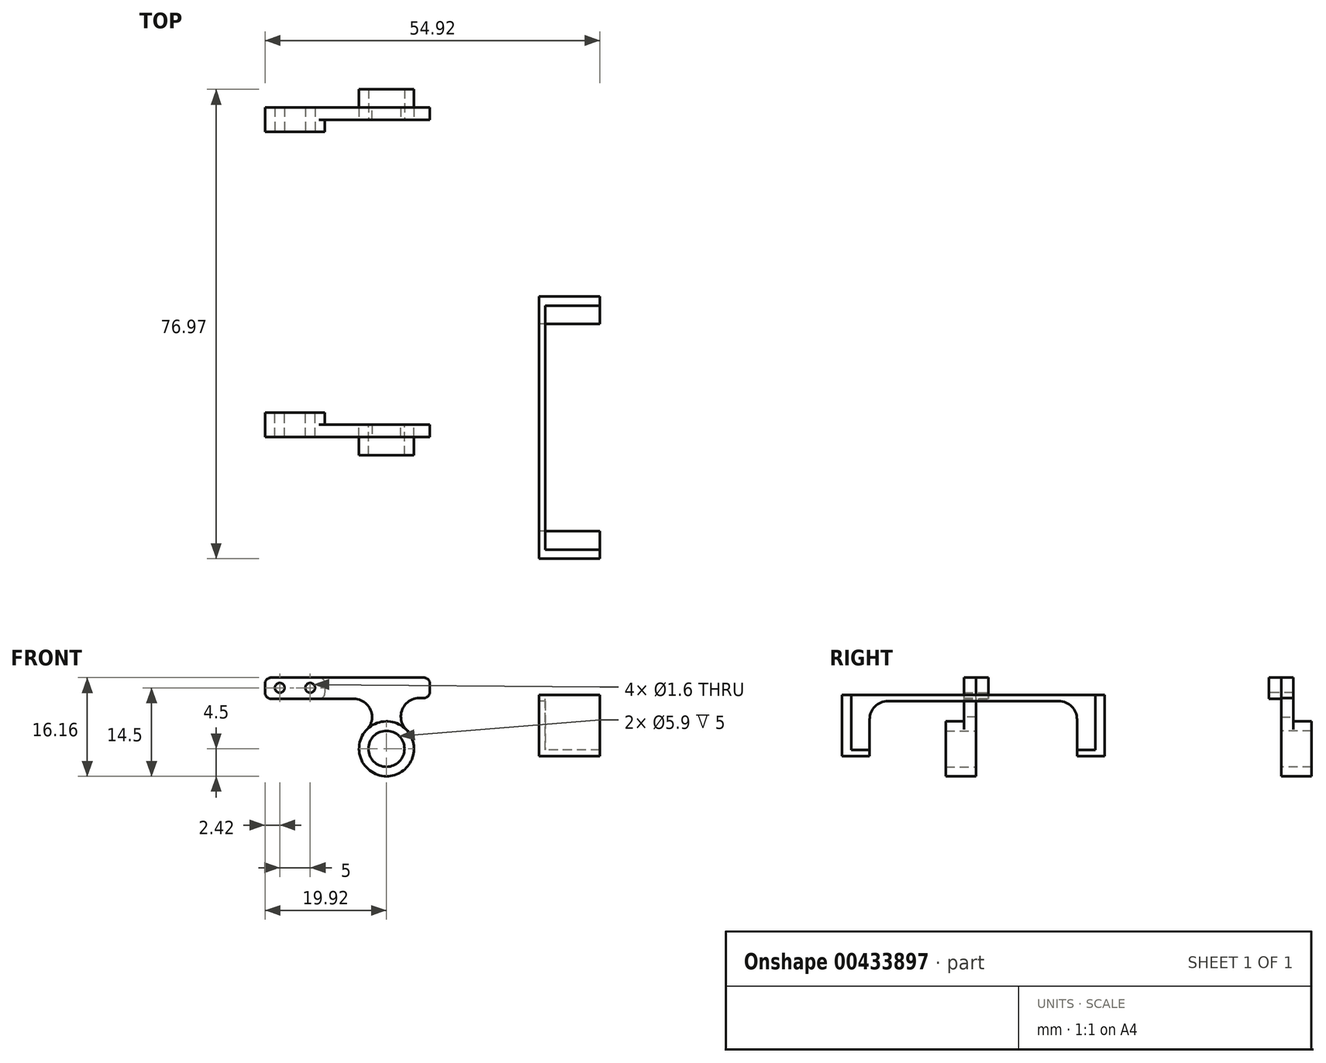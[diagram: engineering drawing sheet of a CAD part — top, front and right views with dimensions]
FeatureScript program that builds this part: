
annotation { "Feature Type Name" : "Feature", "Feature Type Description" : "" }
export const myFeature = defineFeature(function(context is Context, id is Id, definition is map)
    precondition{}
    {
        {
            var Q0;
            Q0=qCreatedBy(makeId("Front.planeOp"),FACE);
            var sketch = newSketch(context, id + "F0", { "sketchPlane" : qUnion([Q0])});
            skCircle(sketch, "E0", {"center": v(0, 0) * mm, "radius": 2.95 * mm});
            skCircle(sketch, "E1", {"center": v(0, 0) * mm, "radius": 4.5 * mm});
            skLineSegment(sketch, "E2", {"start": v(0, 0) * mm, "end": v(-15, 0) * mm, "construction": true});
            skLineSegment(sketch, "E3", {"start": v(-15, 0) * mm, "end": v(-15, 10) * mm, "construction": true});
            skLineSegment(sketch, "E4", {"start": v(-17.5, 10) * mm, "end": v(-12.5, 10) * mm, "construction": true});
            skCircle(sketch, "E5", {"center": v(-17.5, 10) * mm, "radius": 0.8 * mm});
            skCircle(sketch, "E6", {"center": v(-12.5, 10) * mm, "radius": 0.8 * mm});
            skLineSegment(sketch, "E7", {"start": v(-19.92, 11.66) * mm, "end": v(-19.92, 8.2) * mm});
            skLineSegment(sketch, "E8", {"start": v(-19.92, 8.2) * mm, "end": v(-2.36, 8.2) * mm});
            skLineSegment(sketch, "E9", {"start": v(-19.92, 11.66) * mm, "end": v(2.36, 11.66) * mm});
            skLineSegment(sketch, "E10", {"start": v(2.36, 11.66) * mm, "end": v(2.36, 3.83) * mm});
            skLineSegment(sketch, "E11", {"start": v(-2.36, 8.2) * mm, "end": v(-2.36, 3.83) * mm});
            skLineSegment(sketch, "E12", {"start": v(-2.36, 6.63) * mm, "end": v(2.36, 6.63) * mm});
            skPoint(sketch, "E13", {"position": v(0, 6.63) * mm});
            skLineSegment(sketch, "E14.bottom", {"start": v(2.36, 11.66) * mm, "end": v(7.12, 11.66) * mm});
            skLineSegment(sketch, "E14.top", {"start": v(2.36, 8.32) * mm, "end": v(7.12, 8.32) * mm});
            skLineSegment(sketch, "E14.left", {"start": v(2.36, 11.66) * mm, "end": v(2.36, 8.32) * mm});
            skLineSegment(sketch, "E14.right", {"start": v(7.12, 11.66) * mm, "end": v(7.12, 8.32) * mm});
            skSolve(sketch);
        }
        {
            var Q0;
            Q0 = qSketchRegion(id + "F0", true);
            extrude(context, id + "F1", {"entities" : qUnion([Q0]), "depth" : 2 * mm, "offsetDistance" : 25 * mm});
        }
        {
            var Q0;
            Q0=makeQuery(id+"F1.opExtrude","CAP_FACE",FACE,{"disambiguationData":[OSD([sQuery(id+"F0.wireOp",EDGE,"E0"),sQuery(id+"F0.wireOp",EDGE,"E1"),sQuery(id+"F0.wireOp",EDGE,"E5"),sQuery(id+"F0.wireOp",EDGE,"E6"),sQuery(id+"F0.wireOp",EDGE,"E7"),sQuery(id+"F0.wireOp",EDGE,"E8"),sQuery(id+"F0.wireOp",EDGE,"E9"),sQuery(id+"F0.wireOp",EDGE,"E10"),sQuery(id+"F0.wireOp",EDGE,"E11")])],"isStart":true});
            var sketch = newSketch(context, id + "F2", { "sketchPlane" : qUnion([Q0])});
            skLineSegment(sketch, "E15.bottom", {"start": v(19.92, 11.66) * mm, "end": v(10.08, 11.66) * mm});
            skLineSegment(sketch, "E15.top", {"start": v(19.92, 8.2) * mm, "end": v(10.08, 8.2) * mm});
            skLineSegment(sketch, "E15.left", {"start": v(19.92, 11.66) * mm, "end": v(19.92, 8.2) * mm});
            skLineSegment(sketch, "E15.right", {"start": v(10.08, 11.66) * mm, "end": v(10.08, 8.2) * mm});
            skLineSegment(sketch, "E16", {"start": v(12.5, 10) * mm, "end": v(17.5, 10) * mm, "construction": true});
            skPoint(sketch, "E17", {"position": v(15, 10) * mm});
            skPoint(sketch, "E18", {"position": v(15, 11.66) * mm});
            skCircle(sketch, "E19.0", {"center": v(12.5, 10) * mm, "radius": 0.8 * mm});
            skCircle(sketch, "E19.1", {"center": v(17.5, 10) * mm, "radius": 0.8 * mm});
            skSolve(sketch);
        }
        {
            var Q0;
            Q0 = qSketchRegion(id + "F2", true);
            extrude(context, id + "F3", {"entities" : qUnion([Q0]), "operationType" : NewBodyOperationType.ADD, "depth" : 2 * mm, "offsetDistance" : 25 * mm});
        }
        {
            var Q0;
            Q0=makeQuery(id+"F0.imprint","IMPRINT",FACE,{"disambiguationData":[TD([[makeQuery(id+"F0.imprint","IMPRINT",EDGE,{"derivedFrom":sQuery(id+"F0.wireOp",EDGE,"E0")}),-1.0]])]});
            extrude(context, id + "F4", {"entities" : qUnion([Q0]), "operationType" : NewBodyOperationType.ADD, "depth" : 5 * mm, "offsetDistance" : 25 * mm});
        }
        {
            var Q0;
            Q0=makeQuery(id+"F1.opExtrude","SWEPT_EDGE",EDGE,{"disambiguationData":[OSD([sQuery(id+"F0.wireOp",EDGE,"E1"),sQuery(id+"F0.wireOp",EDGE,"E10")])]});
            var Q1;
            Q1=makeQuery(id+"F1.opExtrude","SWEPT_EDGE",EDGE,{"disambiguationData":[OSD([sQuery(id+"F0.wireOp",EDGE,"E8"),sQuery(id+"F0.wireOp",EDGE,"E11")])]});
            var Q2;
            Q2=makeQuery(id+"F1.opExtrude","SWEPT_EDGE",EDGE,{"disambiguationData":[OSD([sQuery(id+"F0.wireOp",EDGE,"E1"),sQuery(id+"F0.wireOp",EDGE,"E11")])]});
            var Q3;
            Q3=makeQuery(id+"F1.opExtrude","SWEPT_EDGE",EDGE,{"disambiguationData":[OSD([sQuery(id+"F0.wireOp",EDGE,"E10"),sQuery(id+"F0.wireOp",EDGE,"E14.top"),sQuery(id+"F0.wireOp",EDGE,"E14.left")])]});
            fillet(context, id + "F5", {"entities" : qUnion([Q0, Q1, Q2, Q3]), "radius" : 3 * mm, "tangentPropagation" : true, "allowEdgeOverflow" : false});
        }
        {
            var Q0;
            Q0=makeQuery(id+"F3.boolean.opBoolean","MERGE",EDGE,{"derivedFrom":[makeQuery(id+"F1.opExtrude","SWEPT_EDGE",EDGE,{"disambiguationData":[OSD([sQuery(id+"F0.wireOp",EDGE,"E7"),sQuery(id+"F0.wireOp",EDGE,"E9")])]}),makeQuery(id+"F3.opExtrude","SWEPT_EDGE",EDGE,{"disambiguationData":[OSD([sQuery(id+"F2.wireOp",EDGE,"E15.bottom"),sQuery(id+"F2.wireOp",EDGE,"E15.left")])]})]});
            var Q1;
            Q1=makeQuery(id+"F3.opExtrude","SWEPT_EDGE",EDGE,{"disambiguationData":[OSD([sQuery(id+"F0.wireOp",EDGE,"E9"),sQuery(id+"F2.wireOp",EDGE,"E15.bottom"),sQuery(id+"F2.wireOp",EDGE,"E15.right")])]});
            var Q2;
            Q2=makeQuery(id+"F3.boolean.opBoolean","MERGE",EDGE,{"derivedFrom":[makeQuery(id+"F1.opExtrude","SWEPT_EDGE",EDGE,{"disambiguationData":[OSD([sQuery(id+"F0.wireOp",EDGE,"E7"),sQuery(id+"F0.wireOp",EDGE,"E8")])]}),makeQuery(id+"F3.opExtrude","SWEPT_EDGE",EDGE,{"disambiguationData":[OSD([sQuery(id+"F2.wireOp",EDGE,"E15.top"),sQuery(id+"F2.wireOp",EDGE,"E15.left")])]})]});
            var Q3;
            Q3=makeQuery(id+"F3.opExtrude","SWEPT_EDGE",EDGE,{"disambiguationData":[OSD([sQuery(id+"F0.wireOp",EDGE,"E8"),sQuery(id+"F2.wireOp",EDGE,"E15.top"),sQuery(id+"F2.wireOp",EDGE,"E15.right")])]});
            var Q4;
            Q4=makeQuery(id+"F1.opExtrude","SWEPT_EDGE",EDGE,{"disambiguationData":[OSD([sQuery(id+"F0.wireOp",EDGE,"E14.top"),sQuery(id+"F0.wireOp",EDGE,"E14.right")])]});
            var Q5;
            Q5=makeQuery(id+"F1.opExtrude","SWEPT_EDGE",EDGE,{"disambiguationData":[OSD([sQuery(id+"F0.wireOp",EDGE,"E14.bottom"),sQuery(id+"F0.wireOp",EDGE,"E14.right")])]});
            fillet(context, id + "F6", {"entities" : qUnion([Q0, Q1, Q2, Q3, Q4, Q5]), "radius" : 1 * mm, "tangentPropagation" : true, "allowEdgeOverflow" : false});
        }
        {
            var Q0;
            Q0=qCreatedBy(makeId("Front.planeOp"),FACE);
            cPlane(context, id + "F7", {"entities" : qUnion([Q0]), "cplaneType" : CPlaneType.OFFSET, "offset" : 25 * mm, "oppositeDirection" : true, "width" : 150 * mm, "height" : 150 * mm});
        }
        {
            var Q0;
            Q0=makeQuery(id+"F1.opExtrude","SWEPT_BODY",BODY,{"disambiguationData":[OSD([sQuery(id+"F0.wireOp",EDGE,"E0"),sQuery(id+"F0.wireOp",EDGE,"E1"),sQuery(id+"F0.wireOp",EDGE,"E5"),sQuery(id+"F0.wireOp",EDGE,"E6"),sQuery(id+"F0.wireOp",EDGE,"E7"),sQuery(id+"F0.wireOp",EDGE,"E8"),sQuery(id+"F0.wireOp",EDGE,"E9"),sQuery(id+"F0.wireOp",EDGE,"E10"),sQuery(id+"F0.wireOp",EDGE,"E11"),sQuery(id+"F0.wireOp",EDGE,"E14.bottom"),sQuery(id+"F0.wireOp",EDGE,"E14.top"),sQuery(id+"F0.wireOp",EDGE,"E14.right")])]});
            var Q1;
            Q1=qCreatedBy(id+"F7.planeOp",FACE);
            mirror(context, id + "F8", {"entities" : qUnion([Q0]), "mirrorPlane" : qUnion([Q1])});
        }
        {
            var Q0;
            Q0=qCreatedBy(makeId("Right.planeOp"),FACE);
            cPlane(context, id + "F9", {"entities" : qUnion([Q0]), "cplaneType" : CPlaneType.OFFSET, "offset" : 25 * mm, "width" : 150 * mm, "height" : 150 * mm});
        }
        {
            var Q0;
            Q0=qCreatedBy(id+"F9.planeOp",FACE);
            var sketch = newSketch(context, id + "F10", { "sketchPlane" : qUnion([Q0])});
            skLineSegment(sketch, "E20.bottom", {"start": v(-21.97, 8.8) * mm, "end": v(-20.47, 8.8) * mm});
            skLineSegment(sketch, "E20.top", {"start": v(-21.97, -1.2) * mm, "end": v(-20.47, -1.2) * mm});
            skLineSegment(sketch, "E20.left", {"start": v(-21.97, 8.8) * mm, "end": v(-21.97, -1.2) * mm});
            skLineSegment(sketch, "E20.right", {"start": v(-20.47, 8.8) * mm, "end": v(-20.47, -1.2) * mm});
            skLineSegment(sketch, "E21.bottom", {"start": v(-20.47, 8.8) * mm, "end": v(19.53, 8.8) * mm});
            skLineSegment(sketch, "E21.top", {"start": v(-20.47, 7.8) * mm, "end": v(19.53, 7.8) * mm});
            skLineSegment(sketch, "E21.left", {"start": v(-20.47, 8.8) * mm, "end": v(-20.47, 7.8) * mm});
            skLineSegment(sketch, "E21.right", {"start": v(19.53, 8.8) * mm, "end": v(19.53, 7.8) * mm});
            skLineSegment(sketch, "E22.bottom", {"start": v(19.53, 8.8) * mm, "end": v(21.03, 8.8) * mm});
            skLineSegment(sketch, "E22.top", {"start": v(19.53, -1.2) * mm, "end": v(21.03, -1.2) * mm});
            skLineSegment(sketch, "E22.left", {"start": v(19.53, 8.8) * mm, "end": v(19.53, -1.2) * mm});
            skLineSegment(sketch, "E22.right", {"start": v(21.03, 8.8) * mm, "end": v(21.03, -1.2) * mm});
            skLineSegment(sketch, "E23.bottom", {"start": v(-20.47, -0.2) * mm, "end": v(-17.47, -0.2) * mm});
            skLineSegment(sketch, "E23.top", {"start": v(-20.47, -1.2) * mm, "end": v(-17.47, -1.2) * mm});
            skLineSegment(sketch, "E23.left", {"start": v(-20.47, -0.2) * mm, "end": v(-20.47, -1.2) * mm});
            skLineSegment(sketch, "E23.right", {"start": v(-17.47, -0.2) * mm, "end": v(-17.47, -1.2) * mm});
            skLineSegment(sketch, "E24.bottom", {"start": v(19.53, -1.2) * mm, "end": v(16.53, -1.2) * mm});
            skLineSegment(sketch, "E24.top", {"start": v(19.53, -0.2) * mm, "end": v(16.53, -0.2) * mm});
            skLineSegment(sketch, "E24.left", {"start": v(19.53, -1.2) * mm, "end": v(19.53, -0.2) * mm});
            skLineSegment(sketch, "E24.right", {"start": v(16.53, -1.2) * mm, "end": v(16.53, -0.2) * mm});
            skLineSegment(sketch, "E25.bottom", {"start": v(-17.47, -0.2) * mm, "end": v(-20.47, -0.2) * mm});
            skLineSegment(sketch, "E25.top", {"start": v(-17.47, 7.8) * mm, "end": v(-20.47, 7.8) * mm});
            skLineSegment(sketch, "E25.left", {"start": v(-17.47, -0.2) * mm, "end": v(-17.47, 7.8) * mm});
            skLineSegment(sketch, "E25.right", {"start": v(-20.47, -0.2) * mm, "end": v(-20.47, 7.8) * mm});
            skLineSegment(sketch, "E26.bottom", {"start": v(19.53, 7.8) * mm, "end": v(16.53, 7.8) * mm});
            skLineSegment(sketch, "E26.left", {"start": v(19.53, 7.8) * mm, "end": v(19.53, -0.2) * mm});
            skLineSegment(sketch, "E26.right", {"start": v(16.53, 7.8) * mm, "end": v(16.53, -0.2) * mm});
            skSolve(sketch);
        }
        {
            var Q0;
            Q0 = qSketchRegion(id + "F10", true);
            extrude(context, id + "F11", {"entities" : qUnion([Q0]), "depth" : 1 * mm, "offsetDistance" : 25 * mm});
        }
        {
            var Q0;
            Q0=makeQuery(id+"F10.imprint","IMPRINT",FACE,{"disambiguationData":[TD([[makeQuery(id+"F10.imprint","IMPRINT",EDGE,{"derivedFrom":sQuery(id+"F10.wireOp",EDGE,"E24.bottom")}),-1.0]])]});
            var Q1;
            Q1=makeQuery(id+"F10.imprint","IMPRINT",FACE,{"disambiguationData":[TD([[makeQuery(id+"F10.imprint","IMPRINT",EDGE,{"derivedFrom":sQuery(id+"F10.wireOp",EDGE,"E23.top")}),1.0]])]});
            var Q2;
            Q2=makeQuery(id+"F10.imprint","IMPRINT",FACE,{"disambiguationData":[TD([[makeQuery(id+"F10.imprint","IMPRINT",EDGE,{"derivedFrom":sQuery(id+"F10.wireOp",EDGE,"E22.bottom")}),-1.0]])]});
            var Q3;
            Q3=makeQuery(id+"F10.imprint","IMPRINT",FACE,{"disambiguationData":[TD([[makeQuery(id+"F10.imprint","IMPRINT",EDGE,{"derivedFrom":sQuery(id+"F10.wireOp",EDGE,"E20.bottom")}),-1.0]])]});
            extrude(context, id + "F12", {"entities" : qUnion([Q0, Q1, Q2, Q3]), "operationType" : NewBodyOperationType.ADD, "depth" : 10 * mm, "offsetDistance" : 25 * mm});
        }
        {
            var Q0;
            Q0=makeQuery(id+"F11.opExtrude","SWEPT_EDGE",EDGE,{"disambiguationData":[OSD([sQuery(id+"F10.wireOp",EDGE,"E21.top"),sQuery(id+"F10.wireOp",EDGE,"E26.bottom"),sQuery(id+"F10.wireOp",EDGE,"E26.right")])]});
            var Q1;
            Q1=makeQuery(id+"F11.opExtrude","SWEPT_EDGE",EDGE,{"disambiguationData":[OSD([sQuery(id+"F10.wireOp",EDGE,"E21.top"),sQuery(id+"F10.wireOp",EDGE,"E25.top"),sQuery(id+"F10.wireOp",EDGE,"E25.left")])]});
            fillet(context, id + "F13", {"entities" : qUnion([Q0, Q1]), "radius" : 3 * mm, "tangentPropagation" : true, "allowEdgeOverflow" : false});
        }
    });
